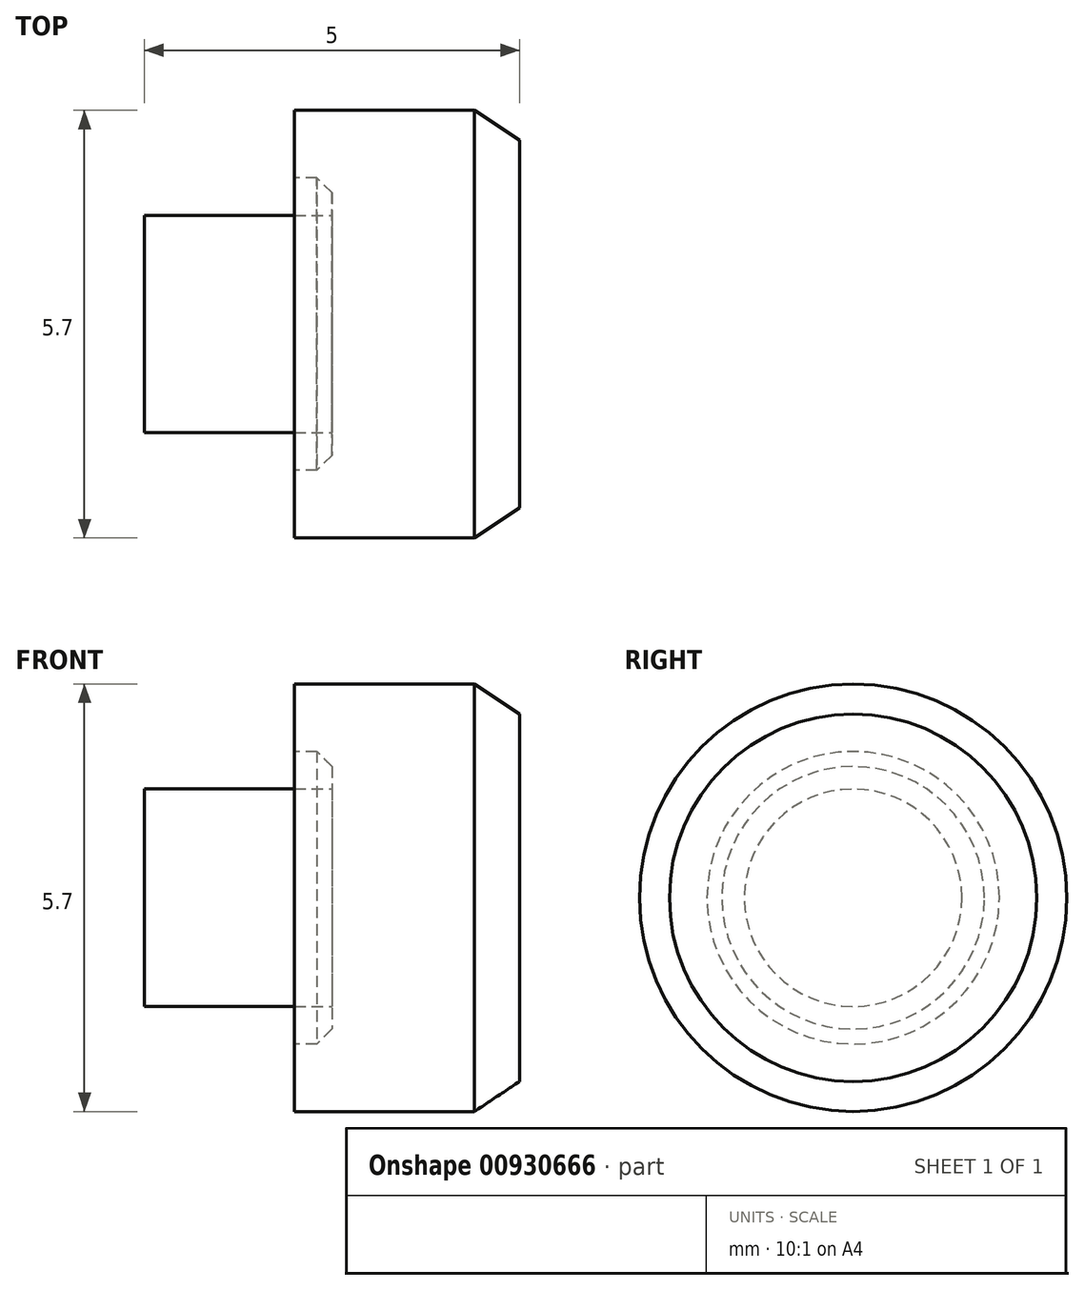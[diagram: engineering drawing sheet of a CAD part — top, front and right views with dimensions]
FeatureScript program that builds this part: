
annotation { "Feature Type Name" : "Feature", "Feature Type Description" : "" }
export const myFeature = defineFeature(function(context is Context, id is Id, definition is map)
    precondition{}
    {
        {
            var Q0;
            Q0=qCreatedBy(makeId("Right.planeOp"),FACE);
            var sketch = newSketch(context, id + "F0", { "sketchPlane" : qUnion([Q0])});
            skCircle(sketch, "E0", {"center": v(0, 0) * mm, "radius": 2.85 * mm});
            skSolve(sketch);
        }
        {
            var Q0;
            Q0=qSketchRegion(id+"F0",true);
            extrude(context, id + "F1", {"entities" : qUnion([Q0]), "depth" : 3 * mm, "offsetDistance" : 25 * mm});
        }
        {
            var Q0;
            Q0=makeQuery(id+"F1.opExtrude","CAP_EDGE",EDGE,{"disambiguationData":[OSD([sQuery(id+"F0.wireOp",EDGE,"E0")])],"isStart":false});
            chamfer(context, id + "F2", {"entities" : qUnion([Q0]), "chamferType" : ChamferType.TWO_OFFSETS, "width1" : 0.4 * mm, "oppositeDirection" : false, "width2" : 0.6 * mm, "tangentPropagation" : true});
        }
        {
            var Q0;
            Q0=makeQuery(id+"F1.opExtrude","CAP_FACE",FACE,{"disambiguationData":[OSD([sQuery(id+"F0.wireOp",EDGE,"E0")])],"isStart":true});
            var sketch = newSketch(context, id + "F3", { "sketchPlane" : qUnion([Q0])});
            skCircle(sketch, "E1", {"center": v(0, 0) * mm, "radius": 1.45 * mm});
            skSolve(sketch);
        }
        {
            var Q0;
            Q0=qSketchRegion(id+"F3",true);
            extrude(context, id + "F4", {"entities" : qUnion([Q0]), "operationType" : NewBodyOperationType.ADD, "depth" : 2 * mm, "offsetDistance" : 25 * mm});
        }
        {
            var Q0;
            Q0=makeQuery(id+"F1.opExtrude","CAP_FACE",FACE,{"disambiguationData":[OSD([sQuery(id+"F0.wireOp",EDGE,"E0")])],"isStart":true});
            var sketch = newSketch(context, id + "F5", { "sketchPlane" : qUnion([Q0])});
            skCircle(sketch, "E2", {"center": v(0, 0) * mm, "radius": 1.95 * mm});
            skCircle(sketch, "E3", {"center": v(0, 0) * mm, "radius": 1.45 * mm});
            skSolve(sketch);
        }
        {
            var Q0;
            Q0=qSketchRegion(id+"F5",true);
            extrude(context, id + "F6", {"entities" : qUnion([Q0]), "operationType" : NewBodyOperationType.REMOVE, "oppositeDirection" : true, "depth" : 0.5 * mm, "offsetDistance" : 25 * mm});
        }
        {
            var Q0;
            Q0=makeQuery(id+"F6.boolean.opBoolean","COPY",EDGE,{"derivedFrom":makeQuery(id+"F6.opExtrude","CAP_EDGE",EDGE,{"disambiguationData":[OSD([sQuery(id+"F5.wireOp",EDGE,"E2")])],"isStart":false})});
            chamfer(context, id + "F7", {"entities" : qUnion([Q0]), "width" : 0.2 * mm, "tangentPropagation" : true});
        }
    });
